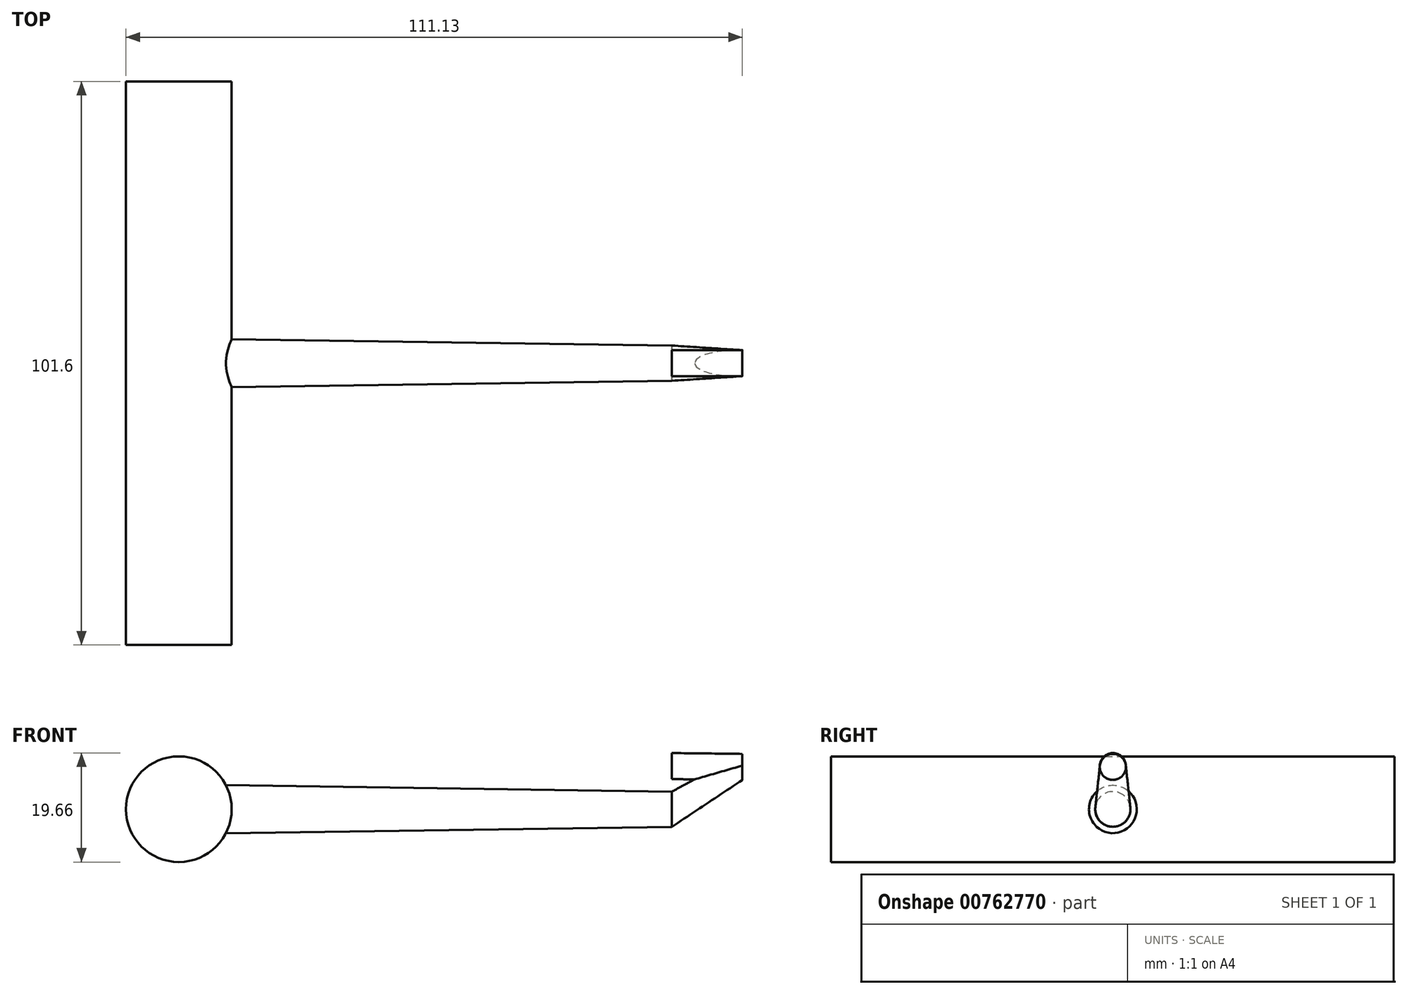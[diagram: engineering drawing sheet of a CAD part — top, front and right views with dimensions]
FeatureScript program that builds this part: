
annotation { "Feature Type Name" : "Feature", "Feature Type Description" : "" }
export const myFeature = defineFeature(function(context is Context, id is Id, definition is map)
    precondition{}
    {
        {
            var Q0;
            Q0=qCreatedBy(makeId("Front.planeOp"),FACE);
            var sketch = newSketch(context, id + "F0", { "sketchPlane" : qUnion([Q0])});
            skCircle(sketch, "E0", {"center": v(0, 0) * mm, "radius": 9.53 * mm});
            skSolve(sketch);
        }
        {
            var Q0;
            Q0=makeQuery(id+"F0.imprint","IMPRINT",FACE,{"disambiguationData":[TD([[makeQuery(id+"F0.imprint","IMPRINT",EDGE,{"derivedFrom":sQuery(id+"F0.wireOp",EDGE,"E0")}),1.0]])]});
            extrude(context, id + "F1", {"entities" : qUnion([Q0]), "depth" : 50.8 * mm, "offsetDistance" : 25.4 * mm, "hasSecondDirection" : true, "secondDirectionOppositeDirection" : true, "secondDirectionDepth" : 50.8 * mm});
        }
        {
            var Q0;
            Q0=qCreatedBy(makeId("Right.planeOp"),FACE);
            var sketch = newSketch(context, id + "F2", { "sketchPlane" : qUnion([Q0])});
            skCircle(sketch, "E1", {"center": v(0, 0) * mm, "radius": 4.45 * mm});
            skSolve(sketch);
        }
        {
            var Q0;
            Q0=qCreatedBy(makeId("Right.planeOp"),FACE);
            cPlane(context, id + "F3", {"entities" : qUnion([Q0]), "cplaneType" : CPlaneType.OFFSET, "offset" : 88.9 * mm, "width" : 152.4 * mm, "height" : 152.4 * mm});
        }
        {
            var Q0;
            Q0=qCreatedBy(id+"F3.planeOp",FACE);
            var sketch = newSketch(context, id + "F4", { "sketchPlane" : qUnion([Q0])});
            skCircle(sketch, "E2", {"center": v(0, 0) * mm, "radius": 3.18 * mm});
            skSolve(sketch);
        }
        {
            var Q1;
            Q1 = qSketchRegion(id + "F2", true);
            var Q2;
            Q2 = qSketchRegion(id + "F4", true);
            loft(context, id + "F5", {"operationType" : NewBodyOperationType.ADD, "sheetProfilesArray" : [{ "sheetProfileEntities" : qUnion([Q1]) }, { "sheetProfileEntities" : qUnion([Q2]) }]});
        }
        {
            var Q0;
            Q0=qCreatedBy(id+"F3.planeOp",FACE);
            cPlane(context, id + "F6", {"entities" : qUnion([Q0]), "cplaneType" : CPlaneType.OFFSET, "offset" : 12.7 * mm, "width" : 152.4 * mm, "height" : 152.4 * mm});
        }
        {
            var Q0;
            Q0=qCreatedBy(id+"F6.planeOp",FACE);
            var sketch = newSketch(context, id + "F7", { "sketchPlane" : qUnion([Q0])});
            skCircle(sketch, "E3", {"center": v(0, 7.62) * mm, "radius": 2.35 * mm});
            skSolve(sketch);
        }
        {
            var Q0;
            Q0=qCreatedBy(id+"F3.planeOp",FACE);
            var sketch = newSketch(context, id + "F8", { "sketchPlane" : qUnion([Q0])});
            skCircle(sketch, "E4", {"center": v(0, 7.78) * mm, "radius": 2.35 * mm});
            skSolve(sketch);
        }
        {
            var Q0;
            Q0=makeQuery(id+"F5.opLoft","CAP_FACE",FACE,{"disambiguationData":[OSD([makeQuery(id+"F4.imprint","IMPRINT",FACE,{"disambiguationData":[TD([[makeQuery(id+"F4.imprint","IMPRINT",EDGE,{"derivedFrom":sQuery(id+"F4.wireOp",EDGE,"E2")}),1.0]])]})])],"isStart":true});
            var Q1;
            Q1=makeQuery(id+"F7.imprint","IMPRINT",FACE,{"disambiguationData":[TD([[makeQuery(id+"F7.imprint","IMPRINT",EDGE,{"derivedFrom":sQuery(id+"F7.wireOp",EDGE,"E3")}),1.0]])]});
            loft(context, id + "F9", {"sheetProfilesArray" : [{ "sheetProfileEntities" : qUnion([Q0]) }, { "sheetProfileEntities" : qUnion([Q1]) }]});
        }
        {
            var Q1;
            Q1=makeQuery(id+"F9.opLoft","CAP_FACE",FACE,{"disambiguationData":[OSD([makeQuery(id+"F7.imprint","IMPRINT",FACE,{"disambiguationData":[TD([[makeQuery(id+"F7.imprint","IMPRINT",EDGE,{"derivedFrom":sQuery(id+"F7.wireOp",EDGE,"E3")}),1.0]])]})])],"isStart":true});
            var Q2;
            Q2=makeQuery(id+"F8.imprint","IMPRINT",FACE,{"disambiguationData":[TD([[makeQuery(id+"F8.imprint","IMPRINT",EDGE,{"derivedFrom":sQuery(id+"F8.wireOp",EDGE,"E4")}),1.0]])]});
            loft(context, id + "F10", {"operationType" : NewBodyOperationType.ADD, "sheetProfilesArray" : [{ "sheetProfileEntities" : qUnion([Q1]) }, { "sheetProfileEntities" : qUnion([Q2]) }]});
        }
    });
